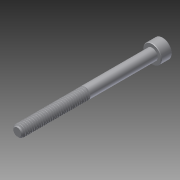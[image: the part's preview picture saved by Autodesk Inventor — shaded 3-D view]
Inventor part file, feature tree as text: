
AUTODESK INVENTOR PART (.ipt)
format: ipt  version: 2015 (Build 190159000, 159)  size: 815,104 bytes
history: native  units: in
note: dims shown in document units (in); Inventor stores cm internally (conversion verified against a paired STEP export)
features: chamfer x1, other x1, imported_body x1
ambient origin geometry x8: Origin, YZ Plane, XZ Plane, XY Plane, X Axis, Y Axis, Z Axis, Center Point
bodies: Body1 (feature_tree)
feature tree (3):
  chamfer  "Chamfer2"  [1 undecoded]
  other  "92196A1331"
  imported_body  "Base1"
note: 1 required parameter value undecoded (feature->parameter linkage not recoverable at this tier; creation-order binding heuristic only, values carry confidence <= 0.55)
